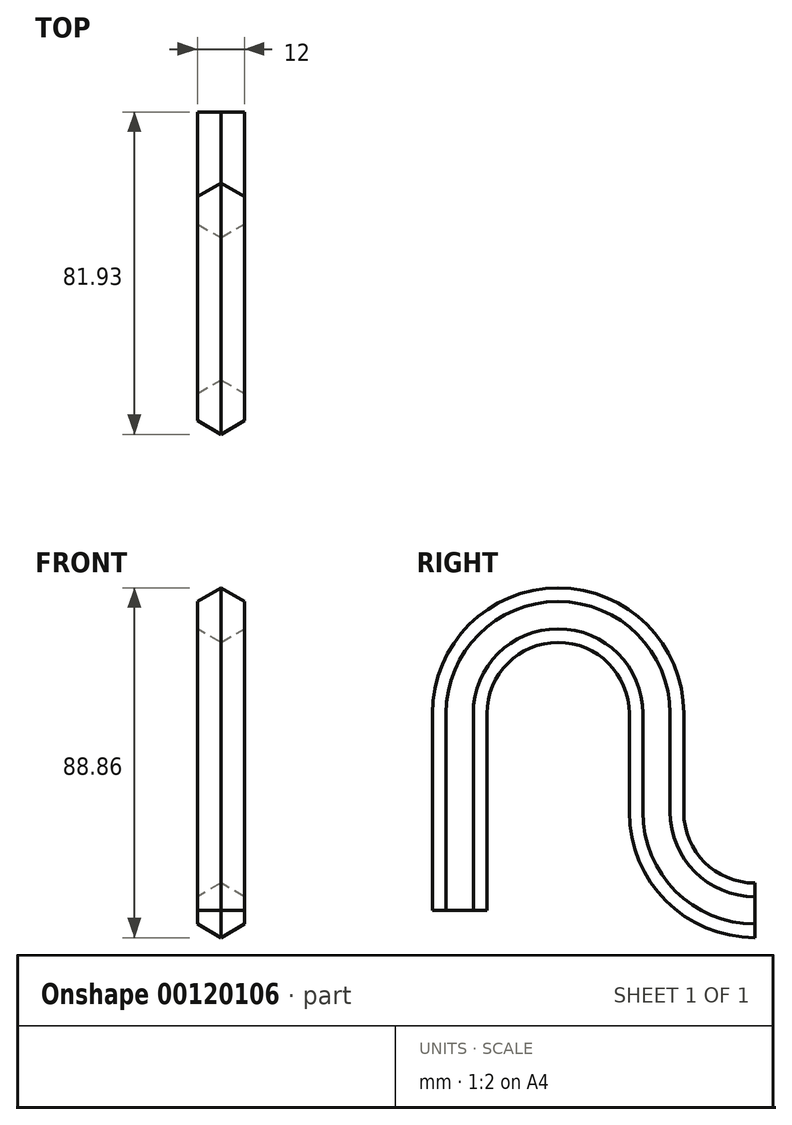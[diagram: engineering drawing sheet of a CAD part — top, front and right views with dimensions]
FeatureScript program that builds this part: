
annotation { "Feature Type Name" : "Feature", "Feature Type Description" : "" }
export const myFeature = defineFeature(function(context is Context, id is Id, definition is map)
    precondition{}
    {
        {
            var Q0;
            Q0=qCreatedBy(makeId("Right.planeOp"),FACE);
            var sketch = newSketch(context, id + "F0", { "sketchPlane" : qUnion([Q0])});
            skLineSegment(sketch, "E0", {"start": v(0, 0) * mm, "end": v(0, 50) * mm});
            skArc(sketch, "E1", {"start": v(0, 50) * mm, "mid": v(25, 75) * mm, "end": v(50, 50) * mm});
            skLineSegment(sketch, "E2", {"start": v(50, 50) * mm, "end": v(50, 25) * mm});
            skArc(sketch, "E3", {"start": v(50, 25) * mm, "mid": v(57.32, 7.32) * mm, "end": v(75, 0) * mm});
            skLineSegment(sketch, "E4", {"start": v(0, 0) * mm, "end": v(112.12, 0) * mm, "construction": true});
            skSolve(sketch);
        }
        {
            var Q0;
            Q0=qCreatedBy(makeId("Top.planeOp"),FACE);
            var sketch = newSketch(context, id + "F1", { "sketchPlane" : qUnion([Q0])});
            skCircle(sketch, "E5.cCircle", {"center": v(0, 0) * mm, "radius": 6 * mm, "construction": true});
            skLineSegment(sketch, "E5.0", {"start": v(6, 3.46) * mm, "end": v(6, -3.46) * mm});
            skLineSegment(sketch, "E5.1", {"start": v(6, -3.46) * mm, "end": v(0, -6.93) * mm});
            skLineSegment(sketch, "E5.2", {"start": v(0, -6.93) * mm, "end": v(-6, -3.46) * mm});
            skLineSegment(sketch, "E5.3", {"start": v(-6, -3.46) * mm, "end": v(-6, 3.46) * mm});
            skLineSegment(sketch, "E5.4", {"start": v(-6, 3.46) * mm, "end": v(0, 6.93) * mm});
            skLineSegment(sketch, "E5.5", {"start": v(0, 6.93) * mm, "end": v(6, 3.46) * mm});
            skPoint(sketch, "E5.0.midPoint", {"position": v(6, 0) * mm});
            skSolve(sketch);
        }
        {
            var Q0;
            Q0=makeQuery(id+"F1.imprint","IMPRINT",FACE,{"disambiguationData":[TD([[makeQuery(id+"F1.imprint","IMPRINT",EDGE,{"derivedFrom":sQuery(id+"F1.wireOp",EDGE,"E5.0")}),-1.0]])]});
            var Q1;
            Q1=sQuery(id+"F0.wireOp",EDGE,"E0");
            var Q2;
            Q2=sQuery(id+"F0.wireOp",EDGE,"E1");
            var Q3;
            Q3=sQuery(id+"F0.wireOp",EDGE,"E2");
            var Q4;
            Q4=sQuery(id+"F0.wireOp",EDGE,"E3");
            sweep(context, id + "F2", {"profiles" : qUnion([Q0]), "path" : qUnion([Q1, Q2, Q3, Q4])});
        }
    });
